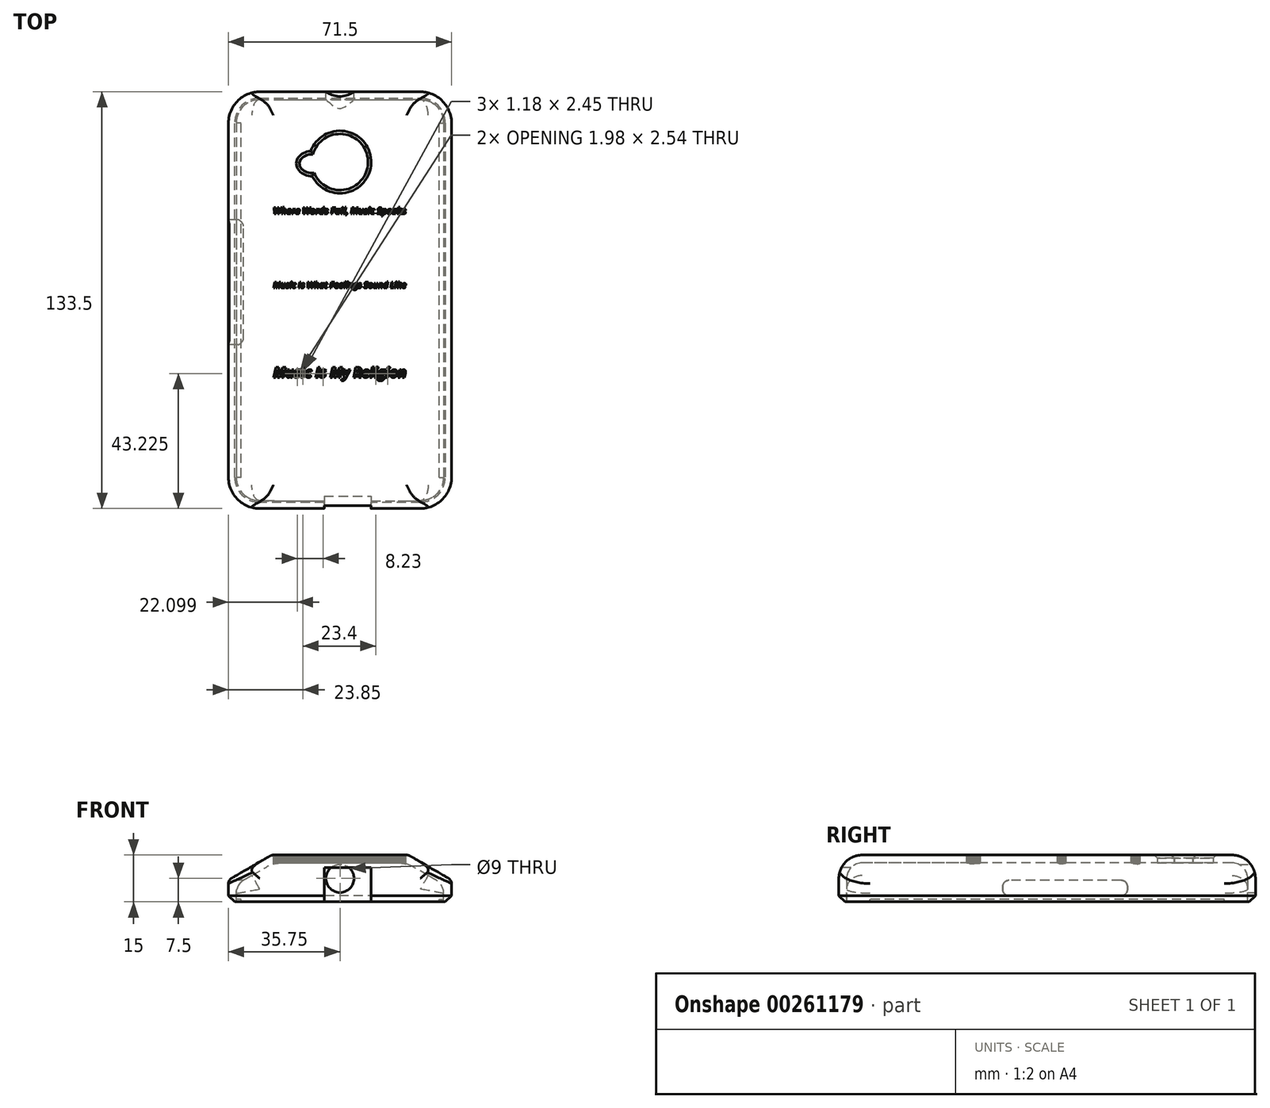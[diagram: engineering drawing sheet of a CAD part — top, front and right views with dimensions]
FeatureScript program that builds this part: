
annotation { "Feature Type Name" : "Feature", "Feature Type Description" : "" }
export const myFeature = defineFeature(function(context is Context, id is Id, definition is map)
    precondition{}
    {
        {
            var Q0;
            Q0=qCreatedBy(makeId("Top.planeOp"),FACE);
            var sketch = newSketch(context, id + "F0", { "sketchPlane" : qUnion([Q0])});
            skLineSegment(sketch, "E0.bottom", {"start": v(0, 0) * mm, "end": v(71.5, 0) * mm});
            skLineSegment(sketch, "E0.top", {"start": v(0, 133.5) * mm, "end": v(71.5, 133.5) * mm});
            skLineSegment(sketch, "E0.left", {"start": v(0, 0) * mm, "end": v(0, 133.5) * mm});
            skLineSegment(sketch, "E0.right", {"start": v(71.5, 0) * mm, "end": v(71.5, 133.5) * mm});
            skSolve(sketch);
        }
        {
            var Q0;
            Q0=qSketchRegion(id+"F0",true);
            extrude(context, id + "F1", {"entities" : qUnion([Q0]), "depth" : 15 * mm});
        }
        {
            var Q0;
            Q0=makeQuery(id+"F1.opExtrude","SWEPT_EDGE",EDGE,{"disambiguationData":[OSD([sQuery(id+"F0.wireOp",EDGE,"E0.top"),sQuery(id+"F0.wireOp",EDGE,"E0.right")])]});
            var Q1;
            Q1=makeQuery(id+"F1.opExtrude","SWEPT_EDGE",EDGE,{"disambiguationData":[OSD([sQuery(id+"F0.wireOp",EDGE,"E0.top"),sQuery(id+"F0.wireOp",EDGE,"E0.left")])]});
            var Q2;
            Q2=makeQuery(id+"F1.opExtrude","SWEPT_EDGE",EDGE,{"disambiguationData":[OSD([sQuery(id+"F0.wireOp",EDGE,"E0.bottom"),sQuery(id+"F0.wireOp",EDGE,"E0.right")])]});
            var Q3;
            Q3=makeQuery(id+"F1.opExtrude","SWEPT_EDGE",EDGE,{"disambiguationData":[OSD([sQuery(id+"F0.wireOp",EDGE,"E0.bottom"),sQuery(id+"F0.wireOp",EDGE,"E0.left")])]});
            fillet(context, id + "F2", {"entities" : qUnion([Q0, Q1, Q2, Q3]), "radius" : 10 * mm, "tangentPropagation" : true, "allowEdgeOverflow" : false});
        }
        {
            var Q0;
            Q0=makeQuery(id+"F1.opExtrude","CAP_EDGE",EDGE,{"disambiguationData":[OSD([sQuery(id+"F0.wireOp",EDGE,"E0.left")])],"isStart":false});
            var Q1;
            Q1=makeQuery(id+"F1.opExtrude","CAP_EDGE",EDGE,{"disambiguationData":[OSD([sQuery(id+"F0.wireOp",EDGE,"E0.right")])],"isStart":false});
            chamfer(context, id + "F3", {"entities" : qUnion([Q0, Q1]), "chamferType" : ChamferType.OFFSET_ANGLE, "width" : 8 * mm, "oppositeDirection" : false, "angle" : 60 * degree});
        }
        {
            var Q0;
            {var subQ0=sQuery(id+"F0.wireOp",EDGE,"E0.left");Q0=makeQuery(id+"F3.opChamfer","BLEND_EDGE",EDGE,{"blendedFrom":[makeQuery(id+"F1.opExtrude","CAP_EDGE",EDGE,{"disambiguationData":[OSD([subQ0])],"isStart":false}),makeQuery(id+"F1.opExtrude","CAP_FACE",FACE,{"disambiguationData":[OSD([sQuery(id+"F0.wireOp",EDGE,"E0.bottom"),sQuery(id+"F0.wireOp",EDGE,"E0.top"),subQ0,sQuery(id+"F0.wireOp",EDGE,"E0.right")])],"isStart":false})],"blendedInto":[makeQuery(id+"F1.opExtrude","CAP_FACE",FACE,{"disambiguationData":[OSD([sQuery(id+"F0.wireOp",EDGE,"E0.bottom"),sQuery(id+"F0.wireOp",EDGE,"E0.top"),subQ0,sQuery(id+"F0.wireOp",EDGE,"E0.right")])],"isStart":false})]});}
            var Q1;
            {var subQ0=sQuery(id+"F0.wireOp",EDGE,"E0.left");Q1=makeQuery(id+"F3.opChamfer","BLEND_EDGE",EDGE,{"blendedFrom":[makeQuery(id+"F1.opExtrude","CAP_EDGE",EDGE,{"disambiguationData":[OSD([subQ0])],"isStart":false}),makeQuery(id+"F1.opExtrude","SWEPT_FACE",FACE,{"disambiguationData":[OSD([subQ0])]})],"blendedInto":[makeQuery(id+"F1.opExtrude","SWEPT_FACE",FACE,{"disambiguationData":[OSD([subQ0])]})]});}
            var Q2;
            {var subQ0=sQuery(id+"F0.wireOp",EDGE,"E0.right");Q2=makeQuery(id+"F3.opChamfer","BLEND_EDGE",EDGE,{"blendedFrom":[makeQuery(id+"F1.opExtrude","CAP_EDGE",EDGE,{"disambiguationData":[OSD([subQ0])],"isStart":false}),makeQuery(id+"F1.opExtrude","CAP_FACE",FACE,{"disambiguationData":[OSD([sQuery(id+"F0.wireOp",EDGE,"E0.bottom"),sQuery(id+"F0.wireOp",EDGE,"E0.top"),sQuery(id+"F0.wireOp",EDGE,"E0.left"),subQ0])],"isStart":false})],"blendedInto":[makeQuery(id+"F1.opExtrude","CAP_FACE",FACE,{"disambiguationData":[OSD([sQuery(id+"F0.wireOp",EDGE,"E0.bottom"),sQuery(id+"F0.wireOp",EDGE,"E0.top"),sQuery(id+"F0.wireOp",EDGE,"E0.left"),subQ0])],"isStart":false})]});}
            var Q3;
            {var subQ0=sQuery(id+"F0.wireOp",EDGE,"E0.right");Q3=makeQuery(id+"F3.opChamfer","BLEND_EDGE",EDGE,{"blendedFrom":[makeQuery(id+"F1.opExtrude","CAP_EDGE",EDGE,{"disambiguationData":[OSD([subQ0])],"isStart":false}),makeQuery(id+"F1.opExtrude","SWEPT_FACE",FACE,{"disambiguationData":[OSD([subQ0])]})],"blendedInto":[makeQuery(id+"F1.opExtrude","SWEPT_FACE",FACE,{"disambiguationData":[OSD([subQ0])]})]});}
            fillet(context, id + "F4", {"entities" : qUnion([Q0, Q1, Q2, Q3]), "radius" : 2 * mm, "tangentPropagation" : true, "allowEdgeOverflow" : false});
        }
        {
            var Q0;
            Q0=makeQuery(id+"F1.opExtrude","CAP_FACE",FACE,{"disambiguationData":[OSD([sQuery(id+"F0.wireOp",EDGE,"E0.bottom"),sQuery(id+"F0.wireOp",EDGE,"E0.top"),sQuery(id+"F0.wireOp",EDGE,"E0.left"),sQuery(id+"F0.wireOp",EDGE,"E0.right")])],"isStart":true});
            shell(context, id + "F5", {"entities" : qUnion([Q0]), "thickness" : 2.5 * mm});
        }
        {
            var Q0;
            {var subQ0=sQuery(id+"F0.wireOp",EDGE,"E0.right");var subQ1=sQuery(id+"F0.wireOp",EDGE,"E0.left");var subQ2=sQuery(id+"F0.wireOp",EDGE,"E0.top");var subQ3=sQuery(id+"F0.wireOp",EDGE,"E0.bottom");var subQ4=makeQuery(id+"F1.opExtrude","CAP_FACE",FACE,{"disambiguationData":[OSD([subQ3,subQ2,subQ1,subQ0])],"isStart":false});var subQ5=makeQuery(id+"F3.opChamfer","BLEND_EDGE",EDGE,{"blendedFrom":[makeQuery(id+"F1.opExtrude","CAP_EDGE",EDGE,{"disambiguationData":[OSD([subQ1])],"isStart":false}),subQ4],"blendedInto":[subQ4]});Q0=makeQuery(id+"F5.opShell","OFFSET_EDGE",EDGE,{"disambiguationData":[OSD([subQ3,subQ2,subQ1,subQ0]),TDD([makeQuery(id+"F4.opFillet","BLEND_EDGE",EDGE,{"blendedFrom":[subQ5,makeQuery(id+"F3.opChamfer","BLEND_FACE",FACE,{"disambiguationData":[OSD([subQ1])]})],"blendedInto":[makeQuery(id+"F3.opChamfer","BLEND_FACE",FACE,{"disambiguationData":[OSD([subQ1])]})]}),makeQuery(id+"F4.opFillet","BLEND_EDGE",EDGE,{"blendedFrom":[subQ5,subQ4],"blendedInto":[subQ4]})])]});}
            var Q1;
            {var subQ0=sQuery(id+"F0.wireOp",EDGE,"E0.right");var subQ1=sQuery(id+"F0.wireOp",EDGE,"E0.left");var subQ2=sQuery(id+"F0.wireOp",EDGE,"E0.top");var subQ3=sQuery(id+"F0.wireOp",EDGE,"E0.bottom");var subQ4=makeQuery(id+"F1.opExtrude","CAP_EDGE",EDGE,{"disambiguationData":[OSD([subQ3])],"isStart":false});Q1=makeQuery(id+"F5.opShell","OFFSET_EDGE",EDGE,{"disambiguationData":[OSD([subQ3,subQ2,subQ1,subQ0]),TDD([makeQuery(id+"F4.opFillet","BLEND_EDGE",EDGE,{"blendedFrom":[subQ4,makeQuery(id+"F1.opExtrude","SWEPT_FACE",FACE,{"disambiguationData":[OSD([subQ3])]})],"blendedInto":[makeQuery(id+"F1.opExtrude","SWEPT_FACE",FACE,{"disambiguationData":[OSD([subQ3])]})]}),makeQuery(id+"F4.opFillet","BLEND_EDGE",EDGE,{"blendedFrom":[subQ4,makeQuery(id+"F1.opExtrude","CAP_FACE",FACE,{"disambiguationData":[OSD([subQ3,subQ2,subQ1,subQ0])],"isStart":false})],"blendedInto":[makeQuery(id+"F1.opExtrude","CAP_FACE",FACE,{"disambiguationData":[OSD([subQ3,subQ2,subQ1,subQ0])],"isStart":false})]})])]});}
            var Q2;
            {var subQ0=sQuery(id+"F0.wireOp",EDGE,"E0.right");var subQ1=sQuery(id+"F0.wireOp",EDGE,"E0.left");var subQ2=sQuery(id+"F0.wireOp",EDGE,"E0.top");var subQ3=sQuery(id+"F0.wireOp",EDGE,"E0.bottom");var subQ4=makeQuery(id+"F1.opExtrude","CAP_FACE",FACE,{"disambiguationData":[OSD([subQ3,subQ2,subQ1,subQ0])],"isStart":false});var subQ5=makeQuery(id+"F3.opChamfer","BLEND_EDGE",EDGE,{"blendedFrom":[makeQuery(id+"F1.opExtrude","CAP_EDGE",EDGE,{"disambiguationData":[OSD([subQ0])],"isStart":false}),subQ4],"blendedInto":[subQ4]});Q2=makeQuery(id+"F5.opShell","OFFSET_EDGE",EDGE,{"disambiguationData":[OSD([subQ3,subQ2,subQ1,subQ0]),TDD([makeQuery(id+"F4.opFillet","BLEND_EDGE",EDGE,{"blendedFrom":[subQ5,makeQuery(id+"F3.opChamfer","BLEND_FACE",FACE,{"disambiguationData":[OSD([subQ0])]})],"blendedInto":[makeQuery(id+"F3.opChamfer","BLEND_FACE",FACE,{"disambiguationData":[OSD([subQ0])]})]}),makeQuery(id+"F4.opFillet","BLEND_EDGE",EDGE,{"blendedFrom":[subQ5,subQ4],"blendedInto":[subQ4]})])]});}
            var Q3;
            {var subQ0=sQuery(id+"F0.wireOp",EDGE,"E0.top");var subQ1=makeQuery(id+"F1.opExtrude","CAP_EDGE",EDGE,{"disambiguationData":[OSD([subQ0])],"isStart":false});var subQ2=sQuery(id+"F0.wireOp",EDGE,"E0.right");var subQ3=sQuery(id+"F0.wireOp",EDGE,"E0.left");var subQ4=sQuery(id+"F0.wireOp",EDGE,"E0.bottom");Q3=makeQuery(id+"F5.opShell","OFFSET_EDGE",EDGE,{"disambiguationData":[OSD([subQ4,subQ0,subQ3,subQ2]),TDD([makeQuery(id+"F4.opFillet","BLEND_EDGE",EDGE,{"blendedFrom":[subQ1,makeQuery(id+"F1.opExtrude","CAP_FACE",FACE,{"disambiguationData":[OSD([subQ4,subQ0,subQ3,subQ2])],"isStart":false})],"blendedInto":[makeQuery(id+"F1.opExtrude","CAP_FACE",FACE,{"disambiguationData":[OSD([subQ4,subQ0,subQ3,subQ2])],"isStart":false})]}),makeQuery(id+"F4.opFillet","BLEND_EDGE",EDGE,{"blendedFrom":[subQ1,makeQuery(id+"F1.opExtrude","SWEPT_FACE",FACE,{"disambiguationData":[OSD([subQ0])]})],"blendedInto":[makeQuery(id+"F1.opExtrude","SWEPT_FACE",FACE,{"disambiguationData":[OSD([subQ0])]})]})])]});}
            fillet(context, id + "F6", {"entities" : qUnion([Q0, Q1, Q2, Q3]), "radius" : 10 * mm, "tangentPropagation" : true, "allowEdgeOverflow" : false});
        }
        {
            var Q0;
            Q0=makeQuery(id+"F1.opExtrude","CAP_EDGE",EDGE,{"disambiguationData":[OSD([sQuery(id+"F0.wireOp",EDGE,"E0.top")])],"isStart":false});
            var Q1;
            Q1=makeQuery(id+"F1.opExtrude","CAP_EDGE",EDGE,{"disambiguationData":[OSD([sQuery(id+"F0.wireOp",EDGE,"E0.bottom")])],"isStart":false});
            fillet(context, id + "F7", {"entities" : qUnion([Q0, Q1]), "radius" : 7.5 * mm, "allowEdgeOverflow" : false});
        }
        {
            var Q0;
            {var subQ0=sQuery(id+"F0.wireOp",EDGE,"E0.bottom");Q0=makeQuery(id+"F5.opShell","OFFSET_EDGE",EDGE,{"disambiguationData":[OSD([subQ0]),TDD([makeQuery(id+"F1.opExtrude","CAP_EDGE",EDGE,{"disambiguationData":[OSD([subQ0])],"isStart":false})])]});}
            fillet(context, id + "F8", {"entities" : qUnion([Q0]), "radius" : 5 * mm, "tangentPropagation" : true, "allowEdgeOverflow" : false});
        }
        {
            var Q0;
            Q0=makeQuery(id+"F1.opExtrude","SWEPT_FACE",FACE,{"disambiguationData":[OSD([sQuery(id+"F0.wireOp",EDGE,"E0.top")])]});
            var sketch = newSketch(context, id + "F9", { "sketchPlane" : qUnion([Q0])});
            skCircle(sketch, "E1", {"center": v(-35.75, 7.5) * mm, "radius": 4.5 * mm});
            skSolve(sketch);
        }
        {
            var Q0;
            Q0=qSketchRegion(id+"F9",true);
            extrude(context, id + "F10", {"entities" : qUnion([Q0]), "operationType" : NewBodyOperationType.REMOVE, "oppositeDirection" : true, "depth" : 25 * mm});
        }
        {
            var Q0;
            Q0=makeQuery(id+"F5.opShell","OFFSET_FACE",FACE,{"disambiguationData":[OSD([sQuery(id+"F0.wireOp",EDGE,"E0.bottom"),sQuery(id+"F0.wireOp",EDGE,"E0.top"),sQuery(id+"F0.wireOp",EDGE,"E0.left"),sQuery(id+"F0.wireOp",EDGE,"E0.right")])]});
            var sketch = newSketch(context, id + "F11", { "sketchPlane" : qUnion([Q0])});
            skCircle(sketch, "E2", {"center": v(35.75, -111) * mm, "radius": 9 * mm});
            skSolve(sketch);
        }
        {
            var Q0;
            Q0=qSketchRegion(id+"F11",true);
            extrude(context, id + "F12", {"entities" : qUnion([Q0]), "operationType" : NewBodyOperationType.REMOVE, "oppositeDirection" : true, "depth" : 25 * mm});
        }
        {
            var Q0;
            Q0=makeQuery(id+"F5.opShell","OFFSET_FACE",FACE,{"disambiguationData":[OSD([sQuery(id+"F0.wireOp",EDGE,"E0.bottom"),sQuery(id+"F0.wireOp",EDGE,"E0.top"),sQuery(id+"F0.wireOp",EDGE,"E0.left"),sQuery(id+"F0.wireOp",EDGE,"E0.right")])]});
            var sketch = newSketch(context, id + "F13", { "sketchPlane" : qUnion([Q0])});
            skEllipse(sketch, "E3", {"center": v(26.76, -110.49) * mm, "majorRadius": 4 * mm, "minorRadius": 3 * mm, "majorAxis": v(-1, 0)});
            skSolve(sketch);
        }
        {
            var Q0;
            Q0=qSketchRegion(id+"F13",true);
            extrude(context, id + "F14", {"entities" : qUnion([Q0]), "operationType" : NewBodyOperationType.REMOVE, "oppositeDirection" : true, "depth" : 25 * mm});
        }
        {
            var Q0;
            Q0=makeQuery(id+"F12.boolean.opBoolean","INTERSECT",EDGE,{"derivedFrom":[makeQuery(id+"F1.opExtrude","CAP_FACE",FACE,{"disambiguationData":[OSD([sQuery(id+"F0.wireOp",EDGE,"E0.bottom"),sQuery(id+"F0.wireOp",EDGE,"E0.top"),sQuery(id+"F0.wireOp",EDGE,"E0.left"),sQuery(id+"F0.wireOp",EDGE,"E0.right")])],"isStart":false}),makeQuery(id+"F12.opExtrude","SWEPT_FACE",FACE,{"disambiguationData":[OSD([sQuery(id+"F11.wireOp",EDGE,"E2")])]})]});
            var Q1;
            Q1=makeQuery(id+"F14.boolean.opBoolean","INTERSECT",EDGE,{"derivedFrom":[makeQuery(id+"F1.opExtrude","CAP_FACE",FACE,{"disambiguationData":[OSD([sQuery(id+"F0.wireOp",EDGE,"E0.bottom"),sQuery(id+"F0.wireOp",EDGE,"E0.top"),sQuery(id+"F0.wireOp",EDGE,"E0.left"),sQuery(id+"F0.wireOp",EDGE,"E0.right")])],"isStart":false}),makeQuery(id+"F14.opExtrude","SWEPT_FACE",FACE,{"disambiguationData":[OSD([sQuery(id+"F13.wireOp",EDGE,"E3")])]})]});
            chamfer(context, id + "F15", {"entities" : qUnion([Q0, Q1]), "width" : 1 * mm, "tangentPropagation" : true});
        }
        {
            var Q0;
            Q0=makeQuery(id+"F1.opExtrude","CAP_EDGE",EDGE,{"disambiguationData":[OSD([sQuery(id+"F0.wireOp",EDGE,"E0.right")])],"isStart":true});
            var Q1;
            Q1=makeQuery(id+"F1.opExtrude","CAP_EDGE",EDGE,{"disambiguationData":[OSD([sQuery(id+"F0.wireOp",EDGE,"E0.top")])],"isStart":true});
            var Q2;
            Q2=makeQuery(id+"F1.opExtrude","CAP_EDGE",EDGE,{"disambiguationData":[OSD([sQuery(id+"F0.wireOp",EDGE,"E0.left")])],"isStart":true});
            var Q3;
            Q3=makeQuery(id+"F1.opExtrude","CAP_EDGE",EDGE,{"disambiguationData":[OSD([sQuery(id+"F0.wireOp",EDGE,"E0.bottom")])],"isStart":true});
            chamfer(context, id + "F16", {"entities" : qUnion([Q0, Q1, Q2, Q3]), "width" : 2 * mm, "tangentPropagation" : true});
        }
        {
            var Q0;
            Q0=makeQuery(id+"F1.opExtrude","SWEPT_FACE",FACE,{"disambiguationData":[OSD([sQuery(id+"F0.wireOp",EDGE,"E0.bottom")])]});
            var sketch = newSketch(context, id + "F17", { "sketchPlane" : qUnion([Q0])});
            skLineSegment(sketch, "E4.bottom", {"start": v(45.7, 0) * mm, "end": v(30.7, 0) * mm});
            skLineSegment(sketch, "E4.top", {"start": v(45.7, 11) * mm, "end": v(30.7, 11) * mm});
            skLineSegment(sketch, "E4.left", {"start": v(45.7, 0) * mm, "end": v(45.7, 11) * mm});
            skLineSegment(sketch, "E4.right", {"start": v(30.7, 0) * mm, "end": v(30.7, 11) * mm});
            skSolve(sketch);
        }
        {
            var Q0;
            Q0=qSketchRegion(id+"F17",true);
            extrude(context, id + "F18", {"entities" : qUnion([Q0]), "operationType" : NewBodyOperationType.REMOVE, "oppositeDirection" : true, "depth" : 25 * mm});
        }
        {
            var Q0;
            {var subQ0=sQuery(id+"F0.wireOp",EDGE,"E0.right");Q0=makeQuery(id+"F5.opShell","OFFSET_FACE",FACE,{"disambiguationData":[OSD([subQ0]),TDD([makeQuery(id+"F1.opExtrude","SWEPT_FACE",FACE,{"disambiguationData":[OSD([subQ0])]})])]});}
            var sketch = newSketch(context, id + "F19", { "sketchPlane" : qUnion([Q0])});
            skLineSegment(sketch, "E5.bottom", {"start": v(-123.5, 0) * mm, "end": v(-10, 0) * mm});
            skLineSegment(sketch, "E5.top", {"start": v(-123.5, 0.75) * mm, "end": v(-10, 0.75) * mm});
            skLineSegment(sketch, "E5.left", {"start": v(-123.5, 0) * mm, "end": v(-123.5, 0.75) * mm});
            skLineSegment(sketch, "E5.right", {"start": v(-10, 0) * mm, "end": v(-10, 0.75) * mm});
            skSolve(sketch);
        }
        {
            var Q0;
            Q0=qSketchRegion(id+"F19",true);
            extrude(context, id + "F20", {"entities" : qUnion([Q0]), "operationType" : NewBodyOperationType.ADD, "depth" : 1.5 * mm});
        }
        {
            var Q0;
            {var subQ0=sQuery(id+"F0.wireOp",EDGE,"E0.left");Q0=makeQuery(id+"F5.opShell","OFFSET_FACE",FACE,{"disambiguationData":[OSD([subQ0]),TDD([makeQuery(id+"F1.opExtrude","SWEPT_FACE",FACE,{"disambiguationData":[OSD([subQ0])]})])]});}
            var sketch = newSketch(context, id + "F21", { "sketchPlane" : qUnion([Q0])});
            skLineSegment(sketch, "E6.bottom", {"start": v(123.5, 0) * mm, "end": v(10, 0) * mm});
            skLineSegment(sketch, "E6.top", {"start": v(123.5, 0.75) * mm, "end": v(10, 0.75) * mm});
            skLineSegment(sketch, "E6.left", {"start": v(123.5, 0) * mm, "end": v(123.5, 0.75) * mm});
            skLineSegment(sketch, "E6.right", {"start": v(10, 0) * mm, "end": v(10, 0.75) * mm});
            skSolve(sketch);
        }
        {
            var Q0;
            Q0=qSketchRegion(id+"F21",true);
            extrude(context, id + "F22", {"entities" : qUnion([Q0]), "operationType" : NewBodyOperationType.ADD, "depth" : 1.5 * mm});
        }
        {
            var Q0;
            Q0=makeQuery(id+"F1.opExtrude","SWEPT_FACE",FACE,{"disambiguationData":[OSD([sQuery(id+"F0.wireOp",EDGE,"E0.left")])]});
            var sketch = newSketch(context, id + "F23", { "sketchPlane" : qUnion([Q0])});
            skLineSegment(sketch, "E7.bottom", {"start": v(-92.5, 2) * mm, "end": v(-52.5, 2) * mm});
            skLineSegment(sketch, "E7.top", {"start": v(-92.5, 6.9) * mm, "end": v(-52.5, 6.9) * mm});
            skLineSegment(sketch, "E7.left", {"start": v(-92.5, 2) * mm, "end": v(-92.5, 6.9) * mm});
            skLineSegment(sketch, "E7.right", {"start": v(-52.5, 2) * mm, "end": v(-52.5, 6.9) * mm});
            skSolve(sketch);
        }
        {
            var Q0;
            Q0=qSketchRegion(id+"F23",true);
            extrude(context, id + "F24", {"entities" : qUnion([Q0]), "operationType" : NewBodyOperationType.REMOVE, "oppositeDirection" : true, "depth" : 25 * mm});
        }
        {
            var Q0;
            Q0=makeQuery(id+"F24.boolean.opBoolean","COPY",EDGE,{"derivedFrom":makeQuery(id+"F24.opExtrude","SWEPT_EDGE",EDGE,{"disambiguationData":[OSD([sQuery(id+"F23.wireOp",EDGE,"E7.top"),sQuery(id+"F23.wireOp",EDGE,"E7.right")])]})});
            var Q1;
            Q1=makeQuery(id+"F24.boolean.opBoolean","COPY",EDGE,{"derivedFrom":makeQuery(id+"F24.opExtrude","SWEPT_EDGE",EDGE,{"disambiguationData":[OSD([sQuery(id+"F0.wireOp",EDGE,"E0.left"),sQuery(id+"F23.wireOp",EDGE,"E7.bottom"),sQuery(id+"F23.wireOp",EDGE,"E7.right")])]})});
            var Q2;
            Q2=makeQuery(id+"F24.boolean.opBoolean","COPY",EDGE,{"derivedFrom":makeQuery(id+"F24.opExtrude","SWEPT_EDGE",EDGE,{"disambiguationData":[OSD([sQuery(id+"F0.wireOp",EDGE,"E0.left"),sQuery(id+"F23.wireOp",EDGE,"E7.bottom"),sQuery(id+"F23.wireOp",EDGE,"E7.left")])]})});
            var Q3;
            Q3=makeQuery(id+"F24.boolean.opBoolean","COPY",EDGE,{"derivedFrom":makeQuery(id+"F24.opExtrude","SWEPT_EDGE",EDGE,{"disambiguationData":[OSD([sQuery(id+"F23.wireOp",EDGE,"E7.top"),sQuery(id+"F23.wireOp",EDGE,"E7.left")])]})});
            fillet(context, id + "F25", {"entities" : qUnion([Q0, Q1, Q2, Q3]), "radius" : 2 * mm, "tangentPropagation" : true, "allowEdgeOverflow" : false});
        }
        {
            var Q0;
            Q0=makeQuery(id+"F1.opExtrude","CAP_FACE",FACE,{"disambiguationData":[OSD([sQuery(id+"F0.wireOp",EDGE,"E0.bottom"),sQuery(id+"F0.wireOp",EDGE,"E0.top"),sQuery(id+"F0.wireOp",EDGE,"E0.left"),sQuery(id+"F0.wireOp",EDGE,"E0.right")])],"isStart":false});
            var sketch = newSketch(context, id + "F26", { "sketchPlane" : qUnion([Q0])});
            skText(sketch, "E8", { "text": "Music Is What Feelings Sound Like", "fontName": "OpenSans-BoldItalic.ttf"});
            const initialGuessF26  = {"E8": [0.0144, 0.07067, 1, 0, 0.00191]};
            skSetInitialGuess(sketch, initialGuessF26);
            skSolve(sketch);
        }
        {
            var Q0;
            Q0=qSketchRegion(id+"F26",true);
            extrude(context, id + "F27", {"entities" : qUnion([Q0]), "operationType" : NewBodyOperationType.REMOVE, "oppositeDirection" : true, "depth" : 25 * mm});
        }
        {
            var Q0;
            {var subQ0=sQuery(id+"F0.wireOp",EDGE,"E0.right");var subQ1=sQuery(id+"F0.wireOp",EDGE,"E0.left");var subQ2=sQuery(id+"F0.wireOp",EDGE,"E0.top");var subQ3=sQuery(id+"F0.wireOp",EDGE,"E0.bottom");var subQ4=makeQuery(id+"F1.opExtrude","CAP_FACE",FACE,{"disambiguationData":[OSD([subQ3,subQ2,subQ1,subQ0])],"isStart":false});Q0=makeQuery(id+"F27.boolean.opBoolean","SPLIT",FACE,{"disambiguationData":[TD([makeQuery(id+"F7.opFillet","BLEND_FACE",FACE,{"disambiguationData":[OSD([subQ3])]})])],"derivedFrom":subQ4});}
            var sketch = newSketch(context, id + "F28", { "sketchPlane" : qUnion([Q0])});
            skText(sketch, "E9", { "text": "Where Words Fail, Music Speaks", "fontName": "OpenSans-BoldItalic.ttf"});
            const initialGuessF28  = {"E9": [0.0144, 0.09436, 1, 0, 0.00203]};
            skSetInitialGuess(sketch, initialGuessF28);
            skSolve(sketch);
        }
        {
            var Q0;
            Q0=qSketchRegion(id+"F28",true);
            extrude(context, id + "F29", {"entities" : qUnion([Q0]), "operationType" : NewBodyOperationType.REMOVE, "oppositeDirection" : true, "depth" : 25 * mm});
        }
        {
            var Q0;
            {var subQ4=sQuery(id+"F0.wireOp",EDGE,"E0.right");var subQ5=sQuery(id+"F0.wireOp",EDGE,"E0.left");var subQ6=sQuery(id+"F0.wireOp",EDGE,"E0.top");var subQ7=sQuery(id+"F0.wireOp",EDGE,"E0.bottom");var subQ8=makeQuery(id+"F1.opExtrude","CAP_FACE",FACE,{"disambiguationData":[OSD([subQ7,subQ6,subQ5,subQ4])],"isStart":false});var subQ199=makeQuery(id+"F7.opFillet","BLEND_FACE",FACE,{"disambiguationData":[OSD([subQ7])]});Q0=makeQuery(id+"F29.boolean.opBoolean","SPLIT",FACE,{"disambiguationData":[TD([subQ199])],"derivedFrom":makeQuery(id+"F27.boolean.opBoolean","SPLIT",FACE,{"disambiguationData":[TD([subQ199])],"derivedFrom":subQ8})});}
            var sketch = newSketch(context, id + "F30", { "sketchPlane" : qUnion([Q0])});
            skText(sketch, "E10", { "text": "Music Is My Religion", "fontName": "OpenSans-BoldItalic.ttf"});
            const initialGuessF30  = {"E10": [0.0144, 0.042, 1, 0, 0.00323]};
            skSetInitialGuess(sketch, initialGuessF30);
            skSolve(sketch);
        }
        {
            var Q0;
            Q0=qSketchRegion(id+"F30",true);
            extrude(context, id + "F31", {"entities" : qUnion([Q0]), "operationType" : NewBodyOperationType.REMOVE, "oppositeDirection" : true, "depth" : 25 * mm});
        }
    });
